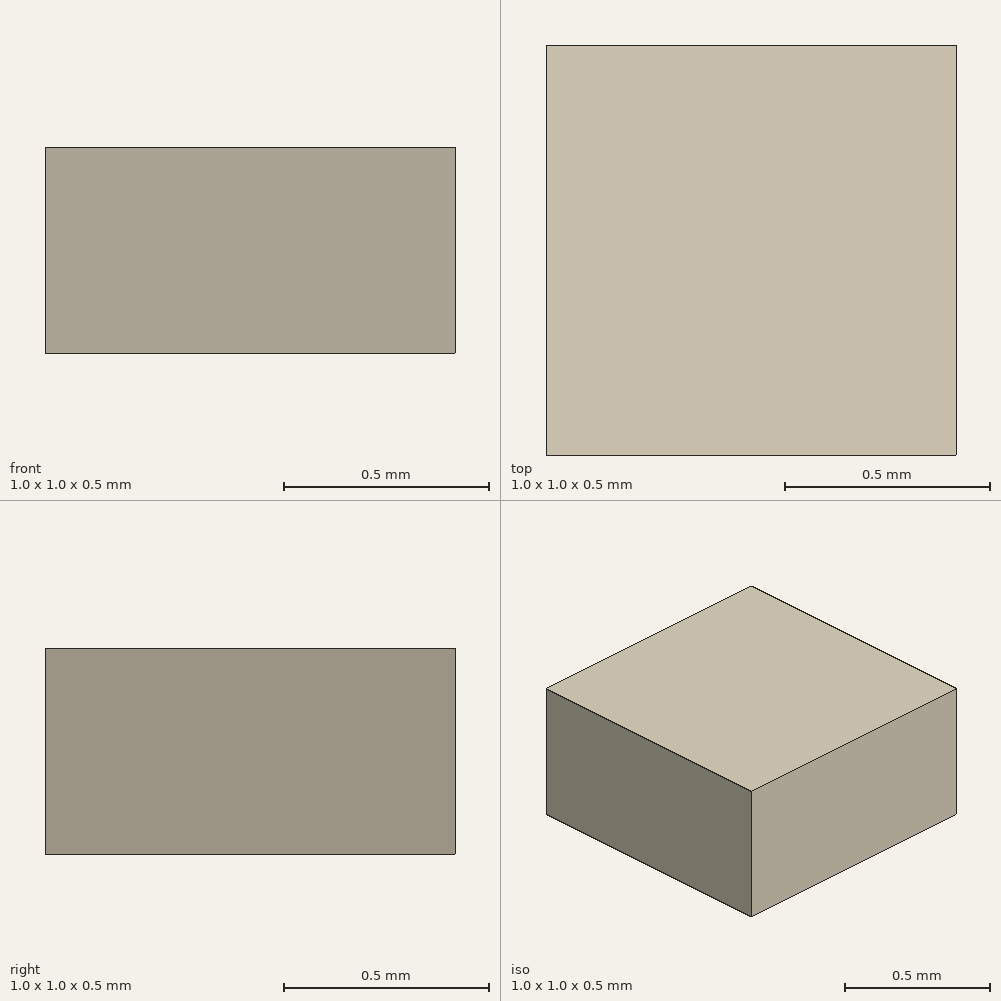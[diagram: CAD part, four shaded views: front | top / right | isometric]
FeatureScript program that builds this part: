
annotation { "Feature Type Name" : "Feature", "Feature Type Description" : "" }
export const myFeature = defineFeature(function(context is Context, id is Id, definition is map)
    precondition{}
    {
        {
            var Q0;
            Q0=qCreatedBy(makeId("Top.planeOp"),FACE);
            var sketch = newSketch(context, id + "F0", { "sketchPlane" : qUnion([Q0])});
            skLineSegment(sketch, "E0.bottom", {"start": v(-0.88, 1.01) * mm, "end": v(0.12, 1.01) * mm});
            skLineSegment(sketch, "E0.top", {"start": v(-0.88, 0.01) * mm, "end": v(0.12, 0.01) * mm});
            skLineSegment(sketch, "E0.left", {"start": v(-0.88, 1.01) * mm, "end": v(-0.88, 0.01) * mm});
            skLineSegment(sketch, "E0.right", {"start": v(0.12, 1.01) * mm, "end": v(0.12, 0.01) * mm});
            skSolve(sketch);
        }
        {
            var Q0;
            Q0=makeQuery(id+"F0.imprint","IMPRINT",FACE,{"disambiguationData":[TD([[makeQuery(id+"F0.imprint","IMPRINT",EDGE,{"derivedFrom":sQuery(id+"F0.wireOp",EDGE,"E0.bottom")}),-1.0]])]});
            extrude(context, id + "F1", {"entities" : qUnion([Q0]), "depth" : .5 * mm});
        }
    });
